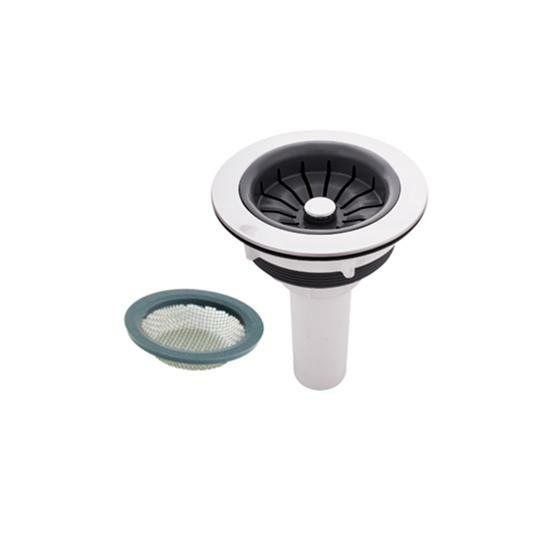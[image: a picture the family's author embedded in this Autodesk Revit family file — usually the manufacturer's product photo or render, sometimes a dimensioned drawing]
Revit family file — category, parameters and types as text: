
# Revit family: L1-3006-11 LAVAPLATOS EN ACERO POCETA 62 X 48 CM
name_source: partatom
category: Aparatos sanitarios
revit_build: Autodesk Revit 2018 (Build: 20170223_1515(x64)
units: mm (PartAtom-declared; Revit-internal decimal feet)

## family parameters
Anfitrión = Cara
Compartido = No
Corte con vacíos al cargar = No
Cota de conector redondo = Diámetro de uso
Número OmniClass = 23.31.11.00
Punto de cálculo de habitación = No
Tipo de pieza = Normal

## types (1)
- L1-3006-11
    Acero inox = Acero inoxidable
    Alto = 160 mm
    Ancho = 620 mm
    Conexión AC = Sí
    Conexión AF = Sí
    Conexión de residuos = No
    Conexión de ventilación = No
    Descripción = Lavaplatos en acero
    Elevación por defecto = 0 mm  [stored 0 ft]
    Fabricante = Gricol
    Imagen de tipo = <Ninguno>
    Largo = 480 mm  [stored 1.5748 ft]
    Link Ficha Tecnica = No existe
    Modelo = L1-3006-11
    Product Name = LAVAPLATOS EN ACERO POCETA 62 X 48 CM
    URL = https://www.gricol.com

note: [stored X ft] marks values corroborated as IEEE doubles in the binary element streams (Revit-internal decimal feet)

## geometry (parser evidence)
native form markers: Blend x2, Sweep x16
no freeform markers — native parametric forms only
